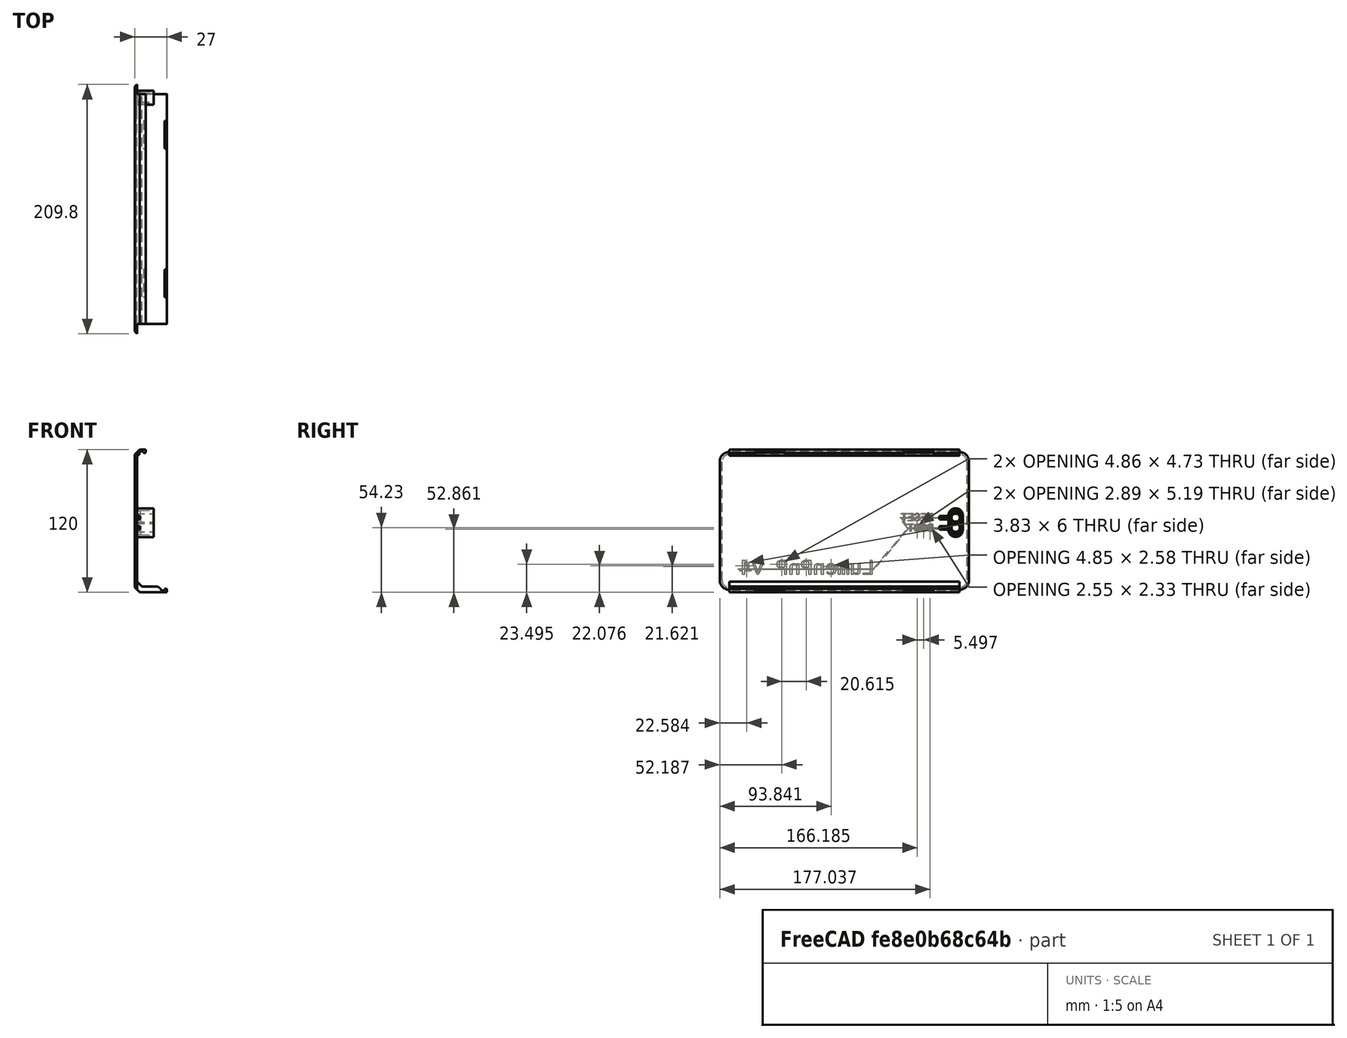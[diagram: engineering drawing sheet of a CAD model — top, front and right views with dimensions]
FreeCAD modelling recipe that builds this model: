
FCSTD DOCUMENT  (FreeCAD 0.20R29603 (Git))
Label: control-box-lid
License: Other
objects: Sketcher::SketchObject×17, PartDesign::Pocket×15, PartDesign::Pad×6, PartDesign::Plane×5, PartDesign::Fillet×5, Part::Part2DObjectPython×3, PartDesign::Mirrored×3, PartDesign::Chamfer×2, PartDesign::SubShapeBinder×2, PartDesign::Body×2, PartDesign::SubtractivePipe×1, Part::Compound×1
note: 91 computed .brp shape members not serialized (recipe doc carries the construction recipe); baked Part::Feature solids carry a one-line shape summary decoded from their .brp

FEATURE [PartDesign::Plane] DatumPlane003  label="Button Strike Plane"
  AttachmentOffset = pos=(0,0,-11.141) rot=(0,0,1;0rad)
  Length = 273.968
  MapMode = 5
  Placement = pos=(0,11.141,2.5e-15) rot=(1,0,0;1.5708rad)
  ResizeMode = 0
  Support = -> [XZ_Plane001]
  Width = 182.068
FEATURE [PartDesign::Plane] DatumPlane004  label="Print Plane"
  AttachmentOffset = pos=(0,0,27) rot=(-0.707107,0,-0.707107;0rad)
  Length = 273.968
  MapMode = 5
  Placement = pos=(0,27,6e-15) rot=(0,0.707107,0.707107;3.14159rad)
  ResizeMode = 0
  Support = -> [XZ_Plane001]
  Width = 182.068
FEATURE [PartDesign::Plane] DatumPlane005
  Length = 69.3666
  MapMode = 5
  Placement = pos=(0,0,0) rot=(0.57735,0.57735,0.57735;2.0944rad)
  ResizeMode = 0
  Support = -> [YZ_Plane001]
  Width = 162.367
FEATURE [Part::Part2DObjectPython] ShapeString  label="LumenPnP Text"  # Draft 2D object (typed FeaturePython)
  AttachmentOffset = pos=(-132,15,0) rot=(0,0,1;0rad)
  FontFile = <userpath>/Github/lumenpnp/lib/fonts/RobotoMono-VariableFont_weight.ttf
  MakeFace = true
  MapMode = 2
  Placement = pos=(132,27,15) rot=(0,0.707107,0.707107;3.14159rad)
  Size = 15
  String = LumenPnP v4
  Support = -> [DatumPlane004]
  Tracking = 0
FEATURE [Part::Part2DObjectPython] ShapeString002  # Draft 2D object (typed FeaturePython)
  AttachmentOffset = pos=(-182,51,0) rot=(0,0,1;0rad)
  FontFile = <userpath>/Github/lumenpnp/lib/fonts/RobotoMono-VariableFont_weight.ttf
  MakeFace = true
  MapMode = 2
  Placement = pos=(182,27,51) rot=(0,0.707107,0.707107;3.14159rad)
  Size = 8
  String = BOOT
  Support = -> [DatumPlane004]
  Tracking = 0
FEATURE [Part::Part2DObjectPython] ShapeString003  # Draft 2D object (typed FeaturePython)
  AttachmentOffset = pos=(-182,60,0) rot=(0,0,1;0rad)
  FontFile = <userpath>/Github/lumenpnp/lib/fonts/RobotoMono-VariableFont_weight.ttf
  MakeFace = true
  MapMode = 2
  Placement = pos=(182,27,60) rot=(0,0.707107,0.707107;3.14159rad)
  Size = 8
  String = RESET
  Support = -> [DatumPlane004]
  Tracking = 0
FEATURE [Sketcher::SketchObject] Sketch
  FullyConstrained = true
  MapMode = 5
  Placement = pos=(0,0,0) rot=(1,0,0;1.5708rad)
  Support = -> [XZ_Plane001]
  sketch-geometry (4):
    g0: LineSegment StartX=0 StartY=0 StartZ=0 EndX=214 EndY=0 EndZ=0
    g1: LineSegment StartX=214 StartY=0 StartZ=0 EndX=214 EndY=120 EndZ=0
    g2: LineSegment StartX=214 StartY=120 StartZ=0 EndX=0 EndY=120 EndZ=0
    g3: LineSegment StartX=0 StartY=120 StartZ=0 EndX=0 EndY=0 EndZ=0
  constraints (11):
    c: Coincident(g0,g1)
    c: Coincident(g1,g2)
    c: Coincident(g2,g3)
    c: Coincident(g3,g0)
    c: Horizontal(g0)
    c: Horizontal(g2)
    c: Vertical(g1)
    c: Vertical(g3)
    c: Coincident(g0,g-1)
    c: DistanceX(g0,g0) = 214
    c: DistanceY(g3,g3) = 120
FEATURE [PartDesign::Pad] Pad  label="Bulk Profile"
  Direction = (0,-1,-2e-16)
  Length = 27
  Length2 = 10
  Placement = pos=(0,0,0) rot=(1,0,0;1.5708rad)
  Profile = -> Sketch
  ReferenceAxis = -> Sketch [N_Axis]
  Reversed = true
  Type = 0
FEATURE [PartDesign::Fillet] Fillet  label="Round Bulk Profile Edges"
  Base = -> Pad [Edge8,Edge5,Edge2,Edge1]
  BaseFeature = -> Pad
  Placement = pos=(0,0,0) rot=(1,0,0;1.5708rad)
  Radius = 10
  SupportTransform = false
  UseAllEdges = false
FEATURE [Sketcher::SketchObject] Sketch001
  ExternalGeometry = -> [Sketch]
  FullyConstrained = true
  MapMode = 5
  Placement = pos=(0,0,0) rot=(1,0,0;1.5708rad)
  Support = -> [XZ_Plane001]
  sketch-geometry (12):
    g0: LineSegment StartX=-50 StartY=109.1 StartZ=0 EndX=250 EndY=109.1 EndZ=0
    g1: LineSegment StartX=250 StartY=109.1 StartZ=0 EndX=250 EndY=10.9 EndZ=0
    g2: LineSegment StartX=250 StartY=10.9 StartZ=0 EndX=-50 EndY=10.9 EndZ=0
    g3: LineSegment StartX=-50 StartY=10.9 StartZ=0 EndX=-50 EndY=109.1 EndZ=0
    g4: ArcOfCircle CenterX=-50 CenterY=109.1 CenterZ=0 NormalX=0 NormalY=0 NormalZ=1 AngleXU=0 Radius=6 StartAngle=1.5708 EndAngle=3.14159
    g5: ArcOfCircle CenterX=250 CenterY=109.1 CenterZ=0 NormalX=0 NormalY=0 NormalZ=1 AngleXU=0 Radius=6 StartAngle=0 EndAngle=1.5708
    g6: ArcOfCircle CenterX=250 CenterY=10.9 CenterZ=0 NormalX=0 NormalY=0 NormalZ=1 AngleXU=0 Radius=6 StartAngle=4.71239 EndAngle=6.28319
    g7: ArcOfCircle CenterX=-50 CenterY=10.9 CenterZ=0 NormalX=0 NormalY=0 NormalZ=1 AngleXU=0 Radius=6 StartAngle=3.14159 EndAngle=4.71239
    g8: LineSegment StartX=-56 StartY=109.1 StartZ=0 EndX=-56 EndY=10.9 EndZ=0
    g9: LineSegment StartX=-50 StartY=4.9 StartZ=0 EndX=250 EndY=4.9 EndZ=0
    g10: LineSegment StartX=256 StartY=10.9 StartZ=0 EndX=256 EndY=109.1 EndZ=0
    g11: LineSegment StartX=250 StartY=115.1 StartZ=0 EndX=-50 EndY=115.1 EndZ=0
  constraints (32):
    c: Coincident(g0,g1)
    c: Coincident(g1,g2)
    c: Coincident(g2,g3)
    c: Coincident(g3,g0)
    c: Horizontal(g0)
    c: Horizontal(g2)
    c: Vertical(g1)
    c: Vertical(g3)
    c: Coincident(g4,g0)
    c: Coincident(g5,g0)
    c: Coincident(g6,g1)
    c: Coincident(g7,g2)
    c: Vertical(g8)
    c: Horizontal(g9)
    c: Vertical(g10)
    c: Tangent(g11,g4) = -1.5708
    c: Tangent(g8,g4) = -1.5708
    c: Tangent(g8,g7) = -1.5708
    c: Tangent(g9,g7) = -1.5708
    c: Tangent(g9,g6) = -1.5708
    c: Tangent(g10,g6) = -1.5708
    c: Tangent(g10,g5) = -1.5708
    c: Tangent(g11,g5) = -1.5708
    c: DistanceX(g2,g2) = 300
    c: DistanceX(g-1,g7) = -50
    c: DistanceY(g-1,g7) = 10.9
    c: DistanceY(g3,g3) = 98.2
    c: Diameter(g4) = 12
    c: DistanceX(g5,g-3) = -42
    c: DistanceX(g-1,g6) = 250
    c: DistanceY(g4,g4) = 6
    c: DistanceY(g7,g7) = 6
FEATURE [PartDesign::Pocket] Pocket  label="Hollow Out Bulk Body"
  BaseFeature = -> Fillet
  Direction = (0,1,2e-16)
  Length = 25
  Length2 = 5
  Placement = pos=(0,0,0) rot=(1,0,0;1.5708rad)
  Profile = -> Sketch001
  ReferenceAxis = -> Sketch001 [N_Axis]
  Type = 0
FEATURE [PartDesign::Chamfer] Chamfer  label="Internal Chamfer"
  Angle = 45
  Base = -> Pocket [Edge21,Edge27]
  BaseFeature = -> Pocket
  ChamferType = 0
  FlipDirection = false
  Placement = pos=(0,0,0) rot=(1,0,0;1.5708rad)
  Size = 4
  Size2 = 1
  SupportTransform = false
  UseAllEdges = false
FEATURE [Sketcher::SketchObject] Sketch011  label="LumenPnP Icon"
  AttachmentOffset = pos=(136,87,-26) rot=(0,0,1;0rad)
  FullyConstrained = true
  MapMode = 5
  Placement = pos=(136,26,87) rot=(1,0,0;1.5708rad)
  Support = -> [XZ_Plane001]
  sketch-geometry (26):
    g0: LineSegment StartX=-123.5 StartY=-76 StartZ=0 EndX=-109.5 EndY=-76 EndZ=0
    g1: LineSegment StartX=-109.5 StartY=-76 StartZ=0 EndX=-109.5 EndY=-60 EndZ=0
    g2: LineSegment StartX=-109.5 StartY=-60 StartZ=0 EndX=14 EndY=-60 EndZ=0
    g3: LineSegment StartX=14 StartY=-60 StartZ=0 EndX=14 EndY=-76 EndZ=0
    g4: LineSegment StartX=14 StartY=-76 StartZ=0 EndX=28 EndY=-76 EndZ=0
    g5: LineSegment StartX=28 StartY=-76 StartZ=0 EndX=28 EndY=-42 EndZ=0
    g6: LineSegment StartX=28 StartY=-42 StartZ=0 EndX=-2.5 EndY=-11.5 EndZ=0
    g7: LineSegment StartX=-2.5 StartY=-11.5 StartZ=0 EndX=-29.75 EndY=-11.5 EndZ=0
    g8: LineSegment StartX=-29.75 StartY=-11.5 StartZ=0 EndX=-29.75 EndY=-1.5 EndZ=0
    g9: LineSegment StartX=-29.75 StartY=-1.5 StartZ=0 EndX=-47.75 EndY=16.5 EndZ=0
    g10: LineSegment StartX=-47.75 StartY=16.5 StartZ=0 EndX=-95 EndY=16.5 EndZ=0
    g11: LineSegment StartX=-123.5 StartY=-76 StartZ=0 EndX=-123.5 EndY=-12 EndZ=0
    g12: LineSegment StartX=-115.5 StartY=-34 StartZ=0 EndX=-115.5 EndY=-12 EndZ=0
    g13: LineSegment StartX=-115.5 StartY=-34 StartZ=0 EndX=-93 EndY=-11.5 EndZ=0
    g14: LineSegment StartX=-93 StartY=-11.5 StartZ=0 EndX=-65.75 EndY=-11.5 EndZ=0
    g15: LineSegment StartX=-65.75 StartY=-11.5 StartZ=0 EndX=-65.75 EndY=-1.5 EndZ=0
    g16: LineSegment StartX=-65.75 StartY=-1.5 StartZ=0 EndX=-55.75 EndY=8.5 EndZ=0
    g17: LineSegment StartX=-55.75 StartY=8.5 StartZ=0 EndX=-95 EndY=8.5 EndZ=0
    g18: ArcOfCircle CenterX=-95 CenterY=-12 CenterZ=0 NormalX=0 NormalY=0 NormalZ=1 AngleXU=0 Radius=20.5 StartAngle=1.5708 EndAngle=3.14159
    g19: ArcOfCircle CenterX=-95 CenterY=-12 CenterZ=0 NormalX=0 NormalY=0 NormalZ=1 AngleXU=0 Radius=28.5 StartAngle=1.5708 EndAngle=3.14159
    g20: Ellipse CenterX=-47.75 CenterY=-38 CenterZ=0 NormalX=0 NormalY=0 NormalZ=1 MajorRadius=19 MinorRadius=8 AngleXU=0
    g21: LineSegment StartX=-28.75 StartY=-38 StartZ=0 EndX=-66.75 EndY=-38 EndZ=0
    g22: LineSegment StartX=-47.75 StartY=-30 StartZ=0 EndX=-47.75 EndY=-46 EndZ=0
    g23: GeomPoint X=-30.5163 Y=-38 Z=0
    g24: GeomPoint X=-64.9837 Y=-38 Z=0
    g25: LineSegment StartX=-47.75 StartY=-60 StartZ=0 EndX=-47.75 EndY=16.5 EndZ=0
  constraints (69):
    c: Horizontal(g0)
    c: Coincident(g0,g1)
    c: Vertical(g1)
    c: Coincident(g1,g2)
    c: Horizontal(g2)
    c: Coincident(g2,g3)
    c: Vertical(g3)
    c: Coincident(g3,g4)
    c: Horizontal(g4)
    c: Coincident(g4,g5)
    c: Vertical(g5)
    c: Coincident(g5,g6)
    c: Coincident(g6,g7)
    c: Horizontal(g7)
    c: Coincident(g7,g8)
    c: Vertical(g8)
    c: Coincident(g8,g9)
    c: Coincident(g9,g10)
    c: Horizontal(g10)
    c: Coincident(g0,g11)
    c: Vertical(g11)
    c: Vertical(g12)
    c: Coincident(g12,g13)
    c: Coincident(g13,g14)
    c: Horizontal(g14)
    c: Coincident(g14,g15)
    c: Vertical(g15)
    c: Coincident(g15,g16)
    c: Coincident(g16,g17)
    c: Horizontal(g17)
    c: Coincident(g18,g17)
    c: Coincident(g18,g12)
    c: Coincident(g19,g10)
    c: Coincident(g19,g11)
    c: InternalAlignment(g21-g24 -> g20) x4
    c: DistanceY(g22,g22) = 16
    c: DistanceX(g21,g21) = 38
    c: Horizontal(g21)
    c: Tangent(g19,g10)
    c: Tangent(g18,g17)
    c: Tangent(g18,g12)
    c: Tangent(g19,g11)
    c: Angle(g9,g8) = 2.35619
    c: Angle(g15,g16) = 2.35619
    c: DistanceX(g0,g0) = 14
    c: DistanceX(g4,g4) = 14
    c: DistanceX(g2,g2) = 123.5
    c: DistanceY(g1,g1) = 16
    c: DistanceY(g3,g3) = 16
    c: DistanceY(g5,g5) = 34
    c: Angle(g6,g5) = 2.35619
    c: DistanceX(g0,g-1) = 123.5
    c: DistanceY(g0,g-1) = 76
    c: Angle(g13,g14) = 2.35619
    c: Coincident(g25,g9)
    c: Vertical(g25)
    c: Symmetric(g1,g2,g25)
    c: PointOnObject(g20,g25)
    c: Distance(g7,g25) = 18
    c: Distance(g14,g25) = 18
    c: PointOnObject(g7,g14)
    c: DistanceY(g0,g13) = 64.5
    c: DistanceX(g0,g12) = 8
    c: DistanceY(g25,g25) = 76.5
    c: Equal(g8,g15)
    c: Coincident(g18,g19)
    c: Diameter(g19) = 57
    c: Equal(g7,g14)
    c: DistanceY(g25,g20) = 22
FEATURE [Sketcher::SketchObject] Sketch013
  FullyConstrained = false
  MapMode = 5
  Placement = pos=(0,11.141,2.5e-15) rot=(0,0.707107,0.707107;3.14159rad)
  Support = -> [DatumPlane003]
  sketch-geometry (2):
    g0: Circle CenterX=-200.672 CenterY=54.1904 CenterZ=0 NormalX=0 NormalY=0 NormalZ=1 AngleXU=0 Radius=3.5
    g1: Circle CenterX=-200.672 CenterY=62.6904 CenterZ=0 NormalX=0 NormalY=0 NormalZ=1 AngleXU=0 Radius=3.5
  constraints (4):
    c: Diameter(g0) = 7
    c: Vertical(g1,g0)
    c: Equal(g0,g1)
    c: DistanceY(g0,g1) = 8.5
FEATURE [PartDesign::Pad] Pad003  label="Button Forming"
  BaseFeature = -> Chamfer
  Direction = (0,1,2e-16)
  Length = 10
  Length2 = 10
  Placement = pos=(0,0,0) rot=(1,0,0;1.5708rad)
  Profile = -> Sketch013
  ReferenceAxis = -> Sketch013 [N_Axis]
  Type = 2
FEATURE [Sketcher::SketchObject] Sketch014
  ExternalGeometry = -> [Pad003]
  FullyConstrained = true
  MapMode = 5
  Placement = pos=(0,11.141,2.5e-15) rot=(1,0,0;1.5708rad)
  Support = -> [DatumPlane003]
  sketch-geometry (20):
    g0: ArcOfCircle CenterX=200.672 CenterY=62.6904 CenterZ=0 NormalX=0 NormalY=0 NormalZ=1 AngleXU=0 Radius=4 StartAngle=3.52599 EndAngle=9.04038
    g1: ArcOfCircle CenterX=200.672 CenterY=62.6904 CenterZ=0 NormalX=0 NormalY=0 NormalZ=1 AngleXU=0 Radius=3.5 StartAngle=3.43134 EndAngle=9.13503
    g2: ArcOfCircle CenterX=200.672 CenterY=54.1904 CenterZ=0 NormalX=0 NormalY=0 NormalZ=1 AngleXU=0 Radius=3.5 StartAngle=3.43134 EndAngle=9.13503
    g3: ArcOfCircle CenterX=200.672 CenterY=54.1904 CenterZ=0 NormalX=0 NormalY=0 NormalZ=1 AngleXU=0 Radius=4 StartAngle=3.52599 EndAngle=9.04038
    g4: ArcOfCircle CenterX=186.964 CenterY=62.6904 CenterZ=0 NormalX=0 NormalY=0 NormalZ=1 AngleXU=0 Radius=1.5 StartAngle=1.5708 EndAngle=4.71239
    g5: LineSegment StartX=186.964 StartY=61.1904 StartZ=0 EndX=196.964 EndY=61.1904 EndZ=0
    g6: ArcOfCircle CenterX=186.964 CenterY=54.1904 CenterZ=0 NormalX=0 NormalY=0 NormalZ=1 AngleXU=0 Radius=1.5 StartAngle=1.5708 EndAngle=4.71239
    g7: LineSegment StartX=196.964 StartY=55.6904 StartZ=0 EndX=186.964 EndY=55.6904 EndZ=0
    g8: LineSegment StartX=186.964 StartY=52.6904 StartZ=0 EndX=196.964 EndY=52.6904 EndZ=0
    g9: LineSegment StartX=196.964 StartY=64.1904 StartZ=0 EndX=186.964 EndY=64.1904 EndZ=0
    g10: ArcOfCircle CenterX=186.964 CenterY=62.6904 CenterZ=0 NormalX=0 NormalY=0 NormalZ=1 AngleXU=0 Radius=1 StartAngle=1.5708 EndAngle=4.71239
    g11: LineSegment StartX=186.964 StartY=61.6904 StartZ=0 EndX=197.318 EndY=61.6904 EndZ=0
    g12: LineSegment StartX=197.318 StartY=63.6904 StartZ=0 EndX=186.964 EndY=63.6904 EndZ=0
    g13: LineSegment StartX=186.964 StartY=63.6904 StartZ=0 EndX=186.964 EndY=64.1904 EndZ=0
    g14: LineSegment StartX=186.964 StartY=61.6904 StartZ=0 EndX=186.964 EndY=61.1904 EndZ=0
    g15: LineSegment StartX=186.964 StartY=62.6904 StartZ=0 EndX=200.672 EndY=62.6904 EndZ=0
    g16: LineSegment StartX=186.964 StartY=53.1904 StartZ=0 EndX=197.318 EndY=53.1904 EndZ=0
    g17: LineSegment StartX=197.318 StartY=55.1904 StartZ=0 EndX=186.964 EndY=55.1904 EndZ=0
    g18: LineSegment StartX=186.964 StartY=55.1904 StartZ=0 EndX=186.964 EndY=55.6904 EndZ=0
    g19: LineSegment StartX=186.964 StartY=53.1904 StartZ=0 EndX=186.964 EndY=52.6904 EndZ=0
  constraints (54):
    c: Coincident(g1,g0)
    c: Coincident(g3,g2)
    c: Equal(g1,g2)
    c: Diameter(g1) = 7
    c: Diameter(g3) = 8
    c: Diameter(g0) = 8
    c: Coincident(g9,g4) = -1.5708
    c: Tangent(g4,g5) = -1.5708
    c: Tangent(g7,g6) = -1.5708
    c: Tangent(g6,g8) = -1.5708
    c: Horizontal(g7)
    c: Equal(g6,g4)
    c: Coincident(g5,g0)
    c: Coincident(g9,g0)
    c: Tangent(g10,g11) = -1.5708
    c: Tangent(g12,g10) = -1.5708
    c: Coincident(g10,g4)
    c: Horizontal(g11)
    c: Coincident(g13,g12)
    c: Coincident(g13,g9)
    c: Vertical(g13)
    c: Coincident(g14,g11)
    c: Coincident(g14,g5)
    c: Vertical(g14)
    c: Coincident(g11,g1)
    c: Horizontal(g9)
    c: DistanceY(g13,g13) = 0.5
    c: Coincident(g15,g4)
    c: Coincident(g15,g0)
    c: Horizontal(g15)
    c: DistanceX(g9,g9) = 10
    c: Diameter(g10) = 2
    c: Vertical(g6,g4)
    c: Coincident(g3,g7)
    c: Coincident(g8,g3)
    c: Equal(g9,g7)
    c: Horizontal(g16)
    c: Horizontal(g17)
    c: Symmetric(g17,g16,g6)
    c: Coincident(g18,g17)
    c: Coincident(g18,g7)
    c: Coincident(g19,g16)
    c: Coincident(g19,g8)
    c: Tangent(g18,g19)
    c: Coincident(g2,g17)
    c: Coincident(g2,g16)
    c: DistanceY(g18,g18) = 0.5
    c: Coincident(g1,g12)
    c: Horizontal(g12)
    c: DistanceY(g2,g0) = 8.5
    c: Vertical(g15,g2)
    c: DistanceX(g-1,g2) = 200.672
    c: DistanceY(g-1,g2) = 54.1904
    c: Coincident(g2,g-3)
FEATURE [PartDesign::Pocket] Pocket016  label="Button Clearance"
  BaseFeature = -> Pad003
  Direction = (0,1,2e-16)
  Length = 40
  Length2 = 5
  Midplane = true
  Placement = pos=(0,0,0) rot=(1,0,0;1.5708rad)
  Profile = -> Sketch014
  ReferenceAxis = -> Sketch014 [N_Axis]
  Type = 0
FEATURE [PartDesign::Pocket] Pocket020  label="Boot"
  BaseFeature = -> Pocket016
  Direction = (0,-1,-2e-16)
  Length = 0.8
  Length2 = 5
  Placement = pos=(0,0,0) rot=(1,0,0;1.5708rad)
  Profile = -> ShapeString002
  ReferenceAxis = -> ShapeString002 [N_Axis]
  Type = 0
FEATURE [PartDesign::Pocket] Pocket021  label="Reset"
  BaseFeature = -> Pocket020
  Direction = (0,-1,-2e-16)
  Length = 0.8
  Length2 = 5
  Placement = pos=(0,0,0) rot=(1,0,0;1.5708rad)
  Profile = -> ShapeString003
  ReferenceAxis = -> ShapeString003 [N_Axis]
  Type = 0
FEATURE [Sketcher::SketchObject] Sketch023
  AttachmentOffset = pos=(0,0,-10.859) rot=(0,0,1;0rad)
  FullyConstrained = true
  MapMode = 5
  Placement = pos=(0,22,4.9e-15) rot=(1,0,0;1.5708rad)
  Support = -> [DatumPlane003]
  sketch-geometry (10):
    g0: LineSegment StartX=186.964 StartY=61.45 StartZ=0 EndX=197.414 EndY=61.45 EndZ=0
    g1: LineSegment StartX=197.414 StartY=61.45 StartZ=0 EndX=197.414 EndY=63.95 EndZ=0
    g2: LineSegment StartX=197.414 StartY=63.95 StartZ=0 EndX=186.964 EndY=63.95 EndZ=0
    g3: LineSegment StartX=186.964 StartY=63.95 StartZ=0 EndX=186.964 EndY=61.45 EndZ=0
    g4: LineSegment StartX=186.964 StartY=52.95 StartZ=0 EndX=197.414 EndY=52.95 EndZ=0
    g5: LineSegment StartX=197.414 StartY=52.95 StartZ=0 EndX=197.414 EndY=55.45 EndZ=0
    g6: LineSegment StartX=197.414 StartY=55.45 StartZ=0 EndX=186.964 EndY=55.45 EndZ=0
    g7: LineSegment StartX=186.964 StartY=55.45 StartZ=0 EndX=186.964 EndY=52.95 EndZ=0
    g8: ArcOfCircle CenterX=200.683 CenterY=54.2 CenterZ=0 NormalX=0 NormalY=0 NormalZ=1 AngleXU=0 Radius=3.5 StartAngle=2.77639 EndAngle=3.5068
    g9: ArcOfCircle CenterX=200.683 CenterY=62.7 CenterZ=0 NormalX=0 NormalY=0 NormalZ=1 AngleXU=0 Radius=3.5 StartAngle=2.77639 EndAngle=3.5068
  constraints (29):
    c: Coincident(g0,g1)
    c: Coincident(g1,g2)
    c: Coincident(g2,g3)
    c: Coincident(g3,g0)
    c: Horizontal(g0)
    c: Horizontal(g2)
    c: Vertical(g1)
    c: Vertical(g3)
    c: Coincident(g4,g5)
    c: Coincident(g5,g6)
    c: Coincident(g6,g7)
    c: Coincident(g7,g4)
    c: Horizontal(g4)
    c: Horizontal(g6)
    c: Vertical(g5)
    c: Coincident(g8,g5)
    c: Coincident(g8,g4)
    c: Coincident(g9,g1)
    c: Coincident(g9,g0)
    c: Equal(g9,g8)
    c: Distance(g7) = 2.5
    c: Equal(g7,g3)
    c: Tangent(g7,g3)
    c: Distance(g4,g0) = 8.5
    c: Vertical(g8,g9)
    c: DistanceX(g2,g2) = 10.45
    c: Diameter(g9) = 7
    c: DistanceX(g-1,g4) = 186.964
    c: DistanceY(g-1,g4) = 52.95
FEATURE [PartDesign::Pocket] Pocket024  label="Make button more bendable"
  BaseFeature = -> Pocket021
  Direction = (0,1,2e-16)
  Length = 3.25
  Length2 = 5
  Placement = pos=(0,0,0) rot=(1,0,0;1.5708rad)
  Profile = -> Sketch023
  ReferenceAxis = -> Sketch023 [N_Axis]
  Type = 0
FEATURE [Sketcher::SketchObject] Sketch024
  ExternalGeometry = -> [Pocket024]
  FullyConstrained = true
  MapMode = 5
  Placement = pos=(0,11.141,2.5e-15) rot=(1,0,0;1.5708rad)
  Support = -> [DatumPlane003]
  sketch-geometry (20):
    g0: ArcOfCircle CenterX=200.672 CenterY=64.5 CenterZ=0 NormalX=0 NormalY=0 NormalZ=1 AngleXU=0 Radius=6 StartAngle=0 EndAngle=3.14159
    g1: ArcOfCircle CenterX=200.672 CenterY=52.5 CenterZ=0 NormalX=0 NormalY=0 NormalZ=1 AngleXU=0 Radius=6 StartAngle=3.14159 EndAngle=6.28319
    g2: LineSegment StartX=194.672 StartY=64.5 StartZ=0 EndX=194.672 EndY=52.5 EndZ=0
    g3: LineSegment StartX=206.672 StartY=52.5 StartZ=0 EndX=206.672 EndY=64.5 EndZ=0
    g4: ArcOfCircle CenterX=200.672 CenterY=64.5 CenterZ=0 NormalX=0 NormalY=0 NormalZ=1 AngleXU=0 Radius=4 StartAngle=9e-16 EndAngle=3.14159
    g5: ArcOfCircle CenterX=200.672 CenterY=52.5 CenterZ=0 NormalX=0 NormalY=0 NormalZ=1 AngleXU=0 Radius=4 StartAngle=3.14159 EndAngle=6.28319
    g6: LineSegment StartX=196.672 StartY=64.5 StartZ=0 EndX=196.672 EndY=52.5 EndZ=0
    g7: LineSegment StartX=204.672 StartY=52.5 StartZ=0 EndX=204.672 EndY=64.5 EndZ=0
    g8: LineSegment StartX=194.672 StartY=64.5 StartZ=0 EndX=206.672 EndY=64.5 EndZ=0
    g9: LineSegment StartX=206.672 StartY=64.5 StartZ=0 EndX=206.672 EndY=66.8 EndZ=0
    g10: LineSegment StartX=202.672 StartY=70.8 StartZ=0 EndX=198.672 EndY=70.8 EndZ=0
    g11: LineSegment StartX=194.672 StartY=66.8 StartZ=0 EndX=194.672 EndY=64.5 EndZ=0
    g12: LineSegment StartX=194.672 StartY=52.5 StartZ=0 EndX=206.672 EndY=52.5 EndZ=0
    g13: LineSegment StartX=206.672 StartY=52.5 StartZ=0 EndX=206.672 EndY=50.2 EndZ=0
    g14: LineSegment StartX=202.672 StartY=46.2 StartZ=0 EndX=198.672 EndY=46.2 EndZ=0
    g15: LineSegment StartX=194.672 StartY=50.2 StartZ=0 EndX=194.672 EndY=52.5 EndZ=0
    g16: ArcOfCircle CenterX=198.672 CenterY=66.8 CenterZ=0 NormalX=0 NormalY=0 NormalZ=1 AngleXU=0 Radius=4 StartAngle=1.5708 EndAngle=3.14159
    g17: ArcOfCircle CenterX=202.672 CenterY=66.8 CenterZ=0 NormalX=0 NormalY=0 NormalZ=1 AngleXU=0 Radius=4 StartAngle=8e-16 EndAngle=1.5708
    g18: ArcOfCircle CenterX=202.672 CenterY=50.2 CenterZ=0 NormalX=0 NormalY=0 NormalZ=1 AngleXU=0 Radius=4 StartAngle=4.71239 EndAngle=6.28319
    g19: ArcOfCircle CenterX=198.672 CenterY=50.2 CenterZ=0 NormalX=0 NormalY=0 NormalZ=1 AngleXU=0 Radius=4 StartAngle=3.14159 EndAngle=4.71239
  constraints (46):
    c: Tangent(g0,g2) = -1.5708
    c: Tangent(g2,g1) = -1.5708
    c: Tangent(g1,g3) = -1.5708
    c: Tangent(g3,g0) = -1.5708
    c: Equal(g0,g1)
    c: Vertical(g2)
    c: Tangent(g4,g6) = -1.5708
    c: Tangent(g6,g5) = -1.5708
    c: Tangent(g5,g7) = -1.5708
    c: Tangent(g7,g4) = -1.5708
    c: Equal(g4,g5)
    c: Coincident(g4,g0)
    c: Coincident(g5,g1)
    c: DistanceX(g0,g4) = 2
    c: Diameter(g4) = 8
    c: DistanceY(g1,g0) = 12
    c: DistanceX(g-1,g1) = 200.672
    c: DistanceY(g-1,g1) = 52.5
    c: Coincident(g8,g9)
    c: Coincident(g11,g8)
    c: Horizontal(g10)
    c: Vertical(g9)
    c: Vertical(g11)
    c: Coincident(g8,g2)
    c: Coincident(g8,g3)
    c: Coincident(g12,g13)
    c: Coincident(g15,g12)
    c: Horizontal(g14)
    c: Vertical(g13)
    c: Vertical(g15)
    c: Coincident(g12,g2)
    c: Coincident(g13,g3)
    c: Tangent(g11,g16) = -1.5708
    c: Tangent(g10,g16) = -1.5708
    c: Tangent(g9,g17) = -1.5708
    c: Tangent(g10,g17) = -1.5708
    c: Tangent(g14,g18) = 1.5708
    c: Tangent(g13,g18) = 1.5708
    c: Tangent(g15,g19) = 1.5708
    c: Tangent(g14,g19) = 1.5708
    c: Equal(g16,g17)
    c: Equal(g17,g18)
    c: Equal(g18,g19)
    c: Diameter(g19) = 8
    c: Equal(g15,g11)
    c: DistanceY(g2,g10) = 6.3
FEATURE [PartDesign::Pad] Pad004  label="Button Shield"
  BaseFeature = -> Pocket024
  Direction = (0,-1,-2e-16)
  Length = 14
  Length2 = 10
  Placement = pos=(0,0,0) rot=(1,0,0;1.5708rad)
  Profile = -> Sketch024
  ReferenceAxis = -> Sketch024 [N_Axis]
  Reversed = true
  Type = 3
  UpToFace = -> Pocket024 [Face2]
FEATURE [Sketcher::SketchObject] Sketch025
  AttachmentOffset = pos=(0,0,-5) rot=(0,0,1;0rad)
  FullyConstrained = true
  MapMode = 5
  Placement = pos=(0,22,4.9e-15) rot=(0,0.707107,0.707107;3.14159rad)
  Support = -> [DatumPlane004]
  sketch-geometry (8):
    g0: LineSegment StartX=-196.964 StartY=64.5 StartZ=0 EndX=-185.964 EndY=64.5 EndZ=0
    g1: LineSegment StartX=-185.964 StartY=64.5 StartZ=0 EndX=-185.964 EndY=60.5 EndZ=0
    g2: LineSegment StartX=-185.964 StartY=60.5 StartZ=0 EndX=-196.964 EndY=60.5 EndZ=0
    g3: LineSegment StartX=-196.964 StartY=60.5 StartZ=0 EndX=-196.964 EndY=64.5 EndZ=0
    g4: LineSegment StartX=-196.964 StartY=56 StartZ=0 EndX=-185.964 EndY=56 EndZ=0
    g5: LineSegment StartX=-185.964 StartY=56 StartZ=0 EndX=-185.964 EndY=52 EndZ=0
    g6: LineSegment StartX=-185.964 StartY=52 StartZ=0 EndX=-196.964 EndY=52 EndZ=0
    g7: LineSegment StartX=-196.964 StartY=52 StartZ=0 EndX=-196.964 EndY=56 EndZ=0
  constraints (23):
    c: Coincident(g0,g1)
    c: Coincident(g1,g2)
    c: Coincident(g2,g3)
    c: Coincident(g3,g0)
    c: Horizontal(g0)
    c: Horizontal(g2)
    c: Vertical(g1)
    c: Vertical(g3)
    c: Coincident(g4,g5)
    c: Coincident(g5,g6)
    c: Coincident(g6,g7)
    c: Coincident(g7,g4)
    c: Horizontal(g4)
    c: Horizontal(g6)
    c: Vertical(g7)
    c: DistanceX(g2,g2) = 11
    c: DistanceY(g1,g1) = 4
    c: Equal(g4,g0)
    c: Equal(g3,g7)
    c: DistanceY(g4,g2) = 4.5
    c: Tangent(g5,g1)
    c: DistanceX(g5,g-1) = 185.964
    c: DistanceY(g-1,g5) = 52
FEATURE [Sketcher::SketchObject] Sketch026
  FullyConstrained = true
  MapMode = 5
  Placement = pos=(0,0,0) rot=(-0.57735,0.57735,0.57735;4.18879rad)
  Support = -> [DatumPlane005]
  sketch-geometry (17):
    g0: LineSegment StartX=0 StartY=3 StartZ=0 EndX=-5 EndY=3 EndZ=0
    g1: LineSegment StartX=-5 StartY=3 StartZ=0 EndX=-5 EndY=5 EndZ=0
    g2: LineSegment StartX=-5 StartY=5 StartZ=0 EndX=0 EndY=5 EndZ=0
    g3: LineSegment StartX=0 StartY=5 StartZ=0 EndX=0 EndY=3 EndZ=0
    g4: ArcOfCircle CenterX=-3.5 CenterY=3 CenterZ=0 NormalX=0 NormalY=0 NormalZ=1 AngleXU=0 Radius=1.5 StartAngle=3.14159 EndAngle=5.79323
    g5: ArcOfCircle CenterX=-1 CenterY=1.66667 CenterZ=0 NormalX=0 NormalY=0 NormalZ=1 AngleXU=0 Radius=1.33333 StartAngle=1.5708 EndAngle=2.65164
    g6: LineSegment StartX=-1 StartY=3 StartZ=0 EndX=0 EndY=3 EndZ=0
    g7: ArcOfCircle CenterX=-3.5 CenterY=3 CenterZ=0 NormalX=0 NormalY=0 NormalZ=1 AngleXU=0 Radius=1.7 StartAngle=3.14159 EndAngle=5.79323
    g8: LineSegment StartX=-2 StartY=2.2 StartZ=0 EndX=-2.17647 EndY=2.29412 EndZ=0
    g9: ArcOfCircle CenterX=-1 CenterY=1.66667 CenterZ=0 NormalX=0 NormalY=0 NormalZ=1 AngleXU=0 Radius=1.13333 StartAngle=1.5708 EndAngle=2.65164
    g10: LineSegment StartX=-1 StartY=2.8 StartZ=0 EndX=0 EndY=2.8 EndZ=0
    g11: LineSegment StartX=0 StartY=2.8 StartZ=0 EndX=0 EndY=5 EndZ=0
    g12: LineSegment StartX=-5.2 StartY=3 StartZ=0 EndX=-5.2 EndY=5 EndZ=0
    g13: LineSegment StartX=-5 StartY=5 StartZ=0 EndX=-5.2 EndY=5 EndZ=0
    g14: LineSegment StartX=-4.70208 StartY=1.79792 StartZ=0 EndX=-7.90416 EndY=5 EndZ=0
    g15: LineSegment StartX=-5.2 StartY=5 StartZ=0 EndX=-7.90416 EndY=5 EndZ=0
    g16: ArcOfCircle CenterX=-3.5 CenterY=3 CenterZ=0 NormalX=0 NormalY=0 NormalZ=1 AngleXU=0 Radius=1.7 StartAngle=3.92699 EndAngle=5.79323
  constraints (47):
    c: Coincident(g0,g1)
    c: Coincident(g1,g2)
    c: Coincident(g2,g3)
    c: Coincident(g3,g0)
    c: Horizontal(g0)
    c: Horizontal(g2)
    c: Vertical(g1)
    c: Vertical(g3)
    c: PointOnObject(g0,g-2)
    c: Coincident(g4,g0)
    c: PointOnObject(g5,g0)
    c: Tangent(g4,g5) = 1.5708
    c: DistanceX(g5,g0) = 1
    c: DistanceX(g2,g2) = 5
    c: DistanceY(g-1,g2) = 5
    c: Vertical(g5,g5)
    c: Perpendicular(g4,g0)
    c: Diameter(g4) = 3
    c: Coincident(g6,g5)
    c: Coincident(g6,g3)
    c: DistanceY(g3,g3) = 2
    c: Coincident(g7,g4)
    c: Coincident(g8,g7)
    c: Coincident(g8,g5)
    c: Perpendicular(g7,g8)
    c: Coincident(g9,g7)
    c: Coincident(g5,g9)
    c: Vertical(g9,g5)
    c: Coincident(g10,g9)
    c: PointOnObject(g10,g-2)
    c: Horizontal(g10)
    c: Coincident(g11,g10)
    c: Coincident(g11,g2)
    c: Vertical(g12)
    c: Coincident(g13,g2)
    c: Coincident(g13,g12)
    c: Horizontal(g13)
    c: Distance(g8) = 0.2
    c: Tangent(g14,g7) = 1.5708
    c: Tangent(g12,g7) = 1.5708
    c: Angle(g14,g0) = 0.785398
    c: Coincident(g15,g12)
    c: Coincident(g15,g14)
    c: Horizontal(g15)
    c: Coincident(g16,g14)
    c: Coincident(g16,g9)
    c: Equal(g16,g7)
FEATURE [Sketcher::SketchObject] Sketch071
  AttachmentOffset = pos=(10,105,0) rot=(0,0,1;0rad)
  FullyConstrained = true
  MapMode = 5
  Placement = pos=(10,-2.33e-14,105) rot=(1,0,0;1.5708rad)
  Support = -> [XZ_Plane001]
  sketch-geometry (40):
    g0: ArcOfCircle CenterX=1.2e-15 CenterY=5 CenterZ=0 NormalX=0 NormalY=0 NormalZ=1 AngleXU=0 Radius=10 StartAngle=1.5708 EndAngle=3.14159
    g1: LineSegment StartX=-4e-16 StartY=15 StartZ=0 EndX=194 EndY=15 EndZ=0
    g2: ArcOfCircle CenterX=194 CenterY=5 CenterZ=0 NormalX=0 NormalY=0 NormalZ=1 AngleXU=0 Radius=10 StartAngle=1e-16 EndAngle=1.5708
    g3: LineSegment StartX=204 StartY=5 StartZ=0 EndX=204 EndY=-95 EndZ=0
    g4: ArcOfCircle CenterX=194 CenterY=-95 CenterZ=0 NormalX=0 NormalY=0 NormalZ=1 AngleXU=0 Radius=10 StartAngle=4.71239 EndAngle=6.28319
    g5: LineSegment StartX=194 StartY=-105 StartZ=0 EndX=0 EndY=-105 EndZ=0
    g6: ArcOfCircle CenterX=1.4e-15 CenterY=-95 CenterZ=0 NormalX=0 NormalY=0 NormalZ=1 AngleXU=0 Radius=10 StartAngle=3.14159 EndAngle=4.71239
    g7: LineSegment StartX=-10 StartY=-95 StartZ=0 EndX=-10 EndY=5 EndZ=0
    g8: GeomPoint X=-10 Y=15 Z=0
    g9: GeomPoint X=204 Y=-105 Z=0
    g10: ArcOfCircle CenterX=1.2e-15 CenterY=5 CenterZ=0 NormalX=0 NormalY=0 NormalZ=1 AngleXU=0 Radius=4.8 StartAngle=1.5708 EndAngle=3.14159
    g11: LineSegment StartX=-10 StartY=5 StartZ=0 EndX=-4.8 EndY=5 EndZ=0
    g12: LineSegment StartX=4e-16 StartY=9.8 StartZ=0 EndX=-4e-16 EndY=15 EndZ=0
    g13: ArcOfCircle CenterX=1.4e-15 CenterY=-95 CenterZ=0 NormalX=0 NormalY=0 NormalZ=1 AngleXU=0 Radius=4.8 StartAngle=3.14159 EndAngle=4.71239
    g14: ArcOfCircle CenterX=194 CenterY=5 CenterZ=0 NormalX=0 NormalY=0 NormalZ=1 AngleXU=0 Radius=4.8 StartAngle=3e-16 EndAngle=1.5708
    g15: ArcOfCircle CenterX=194 CenterY=-95 CenterZ=0 NormalX=0 NormalY=0 NormalZ=1 AngleXU=0 Radius=4.8 StartAngle=4.71239 EndAngle=6.28319
    g16: LineSegment StartX=198.8 StartY=5 StartZ=0 EndX=204 EndY=5 EndZ=0
    g17: LineSegment StartX=198.8 StartY=-95 StartZ=0 EndX=204 EndY=-95 EndZ=0
    g18: LineSegment StartX=-10 StartY=-95 StartZ=0 EndX=-4.8 EndY=-95 EndZ=0
    g19: LineSegment StartX=198.8 StartY=5 StartZ=0 EndX=198.8 EndY=-95 EndZ=0
    g20: LineSegment StartX=5e-16 StartY=-99.8 StartZ=0 EndX=-4e-16 EndY=-105 EndZ=0
    g21: LineSegment StartX=-4.8 StartY=-95 StartZ=0 EndX=-4.8 EndY=5 EndZ=0
    g22: LineSegment StartX=194 StartY=9.8 StartZ=0 EndX=194 EndY=15 EndZ=0
    g23: LineSegment StartX=194 StartY=-99.8 StartZ=0 EndX=194 EndY=-105 EndZ=0
    g24: LineSegment StartX=-4e-16 StartY=15 StartZ=0 EndX=0.2 EndY=15 EndZ=0
    g25: LineSegment StartX=0.2 StartY=15 StartZ=0 EndX=0.2 EndY=9.8 EndZ=0
    g26: LineSegment StartX=0.2 StartY=9.8 StartZ=0 EndX=4e-16 EndY=9.8 EndZ=0
    g27: LineSegment StartX=4e-16 StartY=9.8 StartZ=0 EndX=-4e-16 EndY=15 EndZ=0
    g28: LineSegment StartX=-4e-16 StartY=-105 StartZ=0 EndX=0.2 EndY=-105 EndZ=0
    g29: LineSegment StartX=0.2 StartY=-105 StartZ=0 EndX=0.2 EndY=-99.8 EndZ=0
    g30: LineSegment StartX=0.2 StartY=-99.8 StartZ=0 EndX=5e-16 EndY=-99.8 EndZ=0
    g31: LineSegment StartX=5e-16 StartY=-99.8 StartZ=0 EndX=-4e-16 EndY=-105 EndZ=0
    g32: LineSegment StartX=194 StartY=-99.8 StartZ=0 EndX=193.8 EndY=-99.8 EndZ=0
    g33: LineSegment StartX=193.8 StartY=-99.8 StartZ=0 EndX=193.8 EndY=-105 EndZ=0
    g34: LineSegment StartX=193.8 StartY=-105 StartZ=0 EndX=194 EndY=-105 EndZ=0
    g35: LineSegment StartX=194 StartY=-105 StartZ=0 EndX=194 EndY=-99.8 EndZ=0
    g36: LineSegment StartX=194 StartY=15 StartZ=0 EndX=193.8 EndY=15 EndZ=0
    g37: LineSegment StartX=193.8 StartY=15 StartZ=0 EndX=193.8 EndY=9.8 EndZ=0
    g38: LineSegment StartX=193.8 StartY=9.8 StartZ=0 EndX=194 EndY=9.8 EndZ=0
    g39: LineSegment StartX=194 StartY=9.8 StartZ=0 EndX=194 EndY=15 EndZ=0
  constraints (100):
    c: Tangent(g0,g1) = 1.5708
    c: Tangent(g1,g2) = 1.5708
    c: Tangent(g2,g3) = 1.5708
    c: Tangent(g3,g4) = 1.5708
    c: Tangent(g4,g5) = 1.5708
    c: Tangent(g5,g6) = 1.5708
    c: Tangent(g6,g7) = 1.5708
    c: Tangent(g7,g0) = 1.5708
    c: Horizontal(g1)
    c: Horizontal(g5)
    c: Vertical(g3)
    c: Vertical(g7)
    c: Equal(g0,g2)
    c: Equal(g2,g4)
    c: Equal(g4,g6)
    c: PointOnObject(g8,g1)
    c: PointOnObject(g8,g7)
    c: PointOnObject(g9,g3)
    c: PointOnObject(g9,g5)
    c: Diameter(g0) = 20
    c: PointOnObject(g0,g-2)
    c: DistanceY(g5,g0) = 120
    c: DistanceX(g0,g2) = 214
    c: DistanceY(g-1,g0) = 15
    c: Coincident(g10,g0)
    c: PointOnObject(g10,g-2)
    c: Horizontal(g10,g0)
    c: Coincident(g11,g0)
    c: Coincident(g11,g10)
    c: Coincident(g12,g10)
    c: Coincident(g12,g0)
    c: Diameter(g10) = 9.6
    c: Coincident(g13,g6)
    c: PointOnObject(g13,g-2)
    c: Coincident(g14,g2)
    c: Coincident(g15,g4)
    c: Coincident(g16,g14)
    c: Coincident(g16,g2)
    c: Horizontal(g16)
    c: Coincident(g17,g15)
    c: Coincident(g17,g4)
    c: Horizontal(g17)
    c: Coincident(g18,g6)
    c: Coincident(g18,g13)
    c: Horizontal(g18)
    c: Equal(g10,g14)
    c: Equal(g14,g15)
    c: Equal(g15,g13)
    c: Coincident(g19,g14)
    c: PointOnObject(g19,g15)
    c: Vertical(g19)
    c: Coincident(g20,g13)
    c: Coincident(g20,g6)
    c: Vertical(g20)
    c: Coincident(g21,g13)
    c: Coincident(g21,g10)
    c: Coincident(g22,g14)
    c: Coincident(g22,g2)
    c: Vertical(g22)
    c: Coincident(g23,g15)
    c: Coincident(g23,g4)
    c: Vertical(g23)
    c: Coincident(g24,g25)
    c: Coincident(g25,g26)
    c: Coincident(g26,g27)
    c: Coincident(g27,g24)
    c: Horizontal(g24)
    c: Horizontal(g26)
    c: Vertical(g25)
    c: Coincident(g24,g0)
    c: Coincident(g26,g10)
    c: Coincident(g28,g29)
    c: Coincident(g29,g30)
    c: Coincident(g30,g31)
    c: Coincident(g31,g28)
    c: Horizontal(g28)
    c: Horizontal(g30)
    c: Coincident(g28,g6)
    c: Coincident(g13,g30)
    c: Coincident(g32,g33)
    c: Coincident(g33,g34)
    c: Coincident(g34,g35)
    c: Coincident(g35,g32)
    c: Horizontal(g32)
    c: Horizontal(g34)
    c: Vertical(g33)
    c: Coincident(g32,g15)
    c: Coincident(g34,g4)
    c: Coincident(g36,g37)
    c: Coincident(g37,g38)
    c: Coincident(g38,g39)
    c: Coincident(g39,g36)
    c: Horizontal(g36)
    c: Horizontal(g38)
    c: Coincident(g36,g2)
    c: Coincident(g14,g38)
    c: Tangent(g37,g33)
    c: Tangent(g29,g25)
    c: Equal(g24,g36)
    c: DistanceX(g34,g34) = 0.2
FEATURE [PartDesign::Plane] DatumPlane
  AttachmentOffset = pos=(0,0,107) rot=(0,0,1;0rad)
  Length = 69.3666
  MapMode = 5
  Placement = pos=(107,-2.38e-14,2.38e-14) rot=(0.57735,0.57735,0.57735;2.0944rad)
  ResizeMode = 0
  Support = -> [YZ_Plane001]
  Width = 162.367
FEATURE [PartDesign::Plane] DatumPlane007
  AttachmentOffset = pos=(0,0,60) rot=(0,0,1;0rad)
  Length = 259.098
  MapMode = 5
  Placement = pos=(0,0,60) rot=(0,0,1;0rad)
  ResizeMode = 0
  Support = -> [XY_Plane001]
  Width = 74.198
FEATURE [Sketcher::SketchObject] Sketch068
  AttachmentOffset = pos=(204,-8.2,2.878) rot=(1,0,0;0.593412rad)
  FullyConstrained = false
  MapMode = 5
  Placement = pos=(204,-8.2,2.878) rot=(1,0,0;0.593412rad)
  Support = -> [XY_Plane001]
  sketch-geometry (26):
    g0: LineSegment StartX=-22 StartY=0 StartZ=0 EndX=-47 EndY=0 EndZ=0
    g1: LineSegment StartX=-47 StartY=0 StartZ=0 EndX=-47 EndY=4.5 EndZ=0
    g2: LineSegment StartX=-39.5 StartY=12 StartZ=0 EndX=-29.5 EndY=12 EndZ=0
    g3: LineSegment StartX=-22 StartY=4.5 StartZ=0 EndX=-22 EndY=0 EndZ=0
    g4: LineSegment StartX=-147 StartY=0 StartZ=0 EndX=-172 EndY=0 EndZ=0
    g5: LineSegment StartX=-172 StartY=0 StartZ=0 EndX=-172 EndY=4.5 EndZ=0
    g6: LineSegment StartX=-164.5 StartY=12 StartZ=0 EndX=-154.5 EndY=12 EndZ=0
    g7: LineSegment StartX=-147 StartY=4.5 StartZ=0 EndX=-147 EndY=0 EndZ=0
    g8: ArcOfCircle CenterX=-29.5 CenterY=4.5 CenterZ=0 NormalX=0 NormalY=0 NormalZ=1 AngleXU=0 Radius=7.5 StartAngle=0 EndAngle=1.5708
    g9: GeomPoint X=-22 Y=12 Z=0
    g10: ArcOfCircle CenterX=-39.5 CenterY=4.5 CenterZ=0 NormalX=0 NormalY=0 NormalZ=1 AngleXU=0 Radius=7.5 StartAngle=1.5708 EndAngle=3.14159
    g11: GeomPoint X=-47 Y=12 Z=0
    g12: ArcOfCircle CenterX=-154.5 CenterY=4.5 CenterZ=0 NormalX=0 NormalY=0 NormalZ=1 AngleXU=0 Radius=7.5 StartAngle=0 EndAngle=1.5708
    g13: GeomPoint X=-147 Y=12 Z=0
    g14: ArcOfCircle CenterX=-164.5 CenterY=4.5 CenterZ=0 NormalX=0 NormalY=0 NormalZ=1 AngleXU=0 Radius=7.5 StartAngle=1.5708 EndAngle=3.14159
    g15: GeomPoint X=-172 Y=12 Z=0
    g16: LineSegment StartX=-22 StartY=0 StartZ=0 EndX=-47 EndY=0 EndZ=0
    g17: LineSegment StartX=-47 StartY=0 StartZ=0 EndX=-47 EndY=-3 EndZ=0
    g18: LineSegment StartX=-47 StartY=-3 StartZ=0 EndX=-22 EndY=-3 EndZ=0
    g19: LineSegment StartX=-22 StartY=-3 StartZ=0 EndX=-22 EndY=0 EndZ=0
    g20: LineSegment StartX=-147 StartY=0 StartZ=0 EndX=-172 EndY=0 EndZ=0
    g21: LineSegment StartX=-172 StartY=0 StartZ=0 EndX=-172 EndY=-3 EndZ=0
    g22: LineSegment StartX=-172 StartY=-3 StartZ=0 EndX=-147 EndY=-3 EndZ=0
    g23: LineSegment StartX=-147 StartY=-3 StartZ=0 EndX=-147 EndY=0 EndZ=0
    g24: LineSegment StartX=10 StartY=38 StartZ=0 EndX=-204 EndY=38 EndZ=0
    g25: LineSegment StartX=-97 StartY=38 StartZ=0 EndX=-97 EndY=-62.3515 EndZ=0
  constraints (63):
    c: Coincident(g0,g1)
    c: Coincident(g3,g0)
    c: Horizontal(g0)
    c: Horizontal(g2)
    c: Vertical(g1)
    c: Vertical(g3)
    c: PointOnObject(g0,g-1)
    c: Coincident(g4,g5)
    c: Coincident(g7,g4)
    c: Horizontal(g4)
    c: Horizontal(g6)
    c: Vertical(g5)
    c: Vertical(g7)
    c: PointOnObject(g4,g-1)
    c: PointOnObject(g9,g3)
    c: PointOnObject(g9,g2)
    c: Tangent(g3,g8) = 1.5708
    c: Tangent(g2,g8) = 1.5708
    c: PointOnObject(g11,g2)
    c: PointOnObject(g11,g1)
    c: Tangent(g2,g10) = 1.5708
    c: Tangent(g1,g10) = 1.5708
    c: PointOnObject(g13,g7)
    c: PointOnObject(g13,g6)
    c: Tangent(g7,g12) = 1.5708
    c: Tangent(g6,g12) = 1.5708
    c: PointOnObject(g15,g6)
    c: PointOnObject(g15,g5)
    c: Tangent(g6,g14) = 1.5708
    c: Tangent(g5,g14) = 1.5708
    c: Equal(g14,g12)
    c: Equal(g12,g10)
    c: Equal(g10,g8)
    c: Equal(g3,g2)
    c: Equal(g2,g6)
    c: Equal(g1,g7)
    c: Diameter(g8) = 15
    c: DistanceX(g0,g0) = 25
    c: DistanceY(g0,g2) = 12
    c: Coincident(g16,g17)
    c: Coincident(g17,g18)
    c: Coincident(g18,g19)
    c: Coincident(g19,g16)
    c: Horizontal(g18)
    c: Vertical(g17)
    c: Vertical(g19)
    c: Coincident(g16,g3)
    c: Coincident(g20,g21)
    c: Coincident(g21,g22)
    c: Coincident(g22,g23)
    c: Coincident(g23,g20)
    c: Vertical(g21)
    c: Vertical(g23)
    c: Coincident(g20,g7)
    c: Coincident(g5,g21)
    c: Coincident(g1,g17)
    c: Tangent(g22,g18)
    c: DistanceY(g-1,g17) = -3
    c: DistanceX(g22,g17) = 100
    c: DistanceX(g-1,g24) = 10
    c: DistanceX(g24,g24) = 214
    c: Symmetric(g24,g24,g25)
    c: Symmetric(g1,g7,g25)
FEATURE [PartDesign::Pocket] Pocket029
  BaseFeature = -> Pad004
  Direction = (0,-1,6e-16)
  Length = 2
  Length2 = 5
  Placement = pos=(0,0,0) rot=(1,0,0;1.5708rad)
  Profile = -> Pad004 [Face221,Face218]
  Type = 0
FEATURE [PartDesign::Chamfer] Chamfer001
  Angle = 3
  Base = -> Pocket029 [Edge684]
  BaseFeature = -> Pocket029
  ChamferType = 2
  FlipDirection = true
  Placement = pos=(0,0,0) rot=(1,0,0;1.5708rad)
  Size = 11
  Size2 = 1
  SupportTransform = false
  UseAllEdges = false
FEATURE [PartDesign::Pocket] Pocket025  label="Locking Lip"
  BaseFeature = -> Chamfer001
  Direction = (1,-1e-16,1e-16)
  Length = 5
  Length2 = 5
  Placement = pos=(0,0,0) rot=(1,0,0;1.5708rad)
  Profile = -> Sketch026
  ReferenceAxis = -> Sketch026 [N_Axis]
  Type = 1
FEATURE [PartDesign::Pocket] Pocket026  label="Removing Side"
  BaseFeature = -> Pocket025
  Direction = (0,1,2e-16)
  Length = 25
  Length2 = 5
  Placement = pos=(0,0,0) rot=(1,0,0;1.5708rad)
  Profile = -> Sketch071
  ReferenceAxis = -> Sketch071 [N_Axis]
  Type = 0
FEATURE [PartDesign::Mirrored] Mirrored001  label="Mirrors Removing Side"
  BaseFeature = -> Pocket026
  MirrorPlane = -> DatumPlane
  Originals = -> [Pocket026]
  Placement = pos=(0,0,0) rot=(1,0,0;1.5708rad)
FEATURE [PartDesign::Mirrored] Mirrored002  label="Mirrors Locking Lip"
  BaseFeature = -> Mirrored001
  MirrorPlane = -> DatumPlane007
  Originals = -> [Pocket025]
  Placement = pos=(0,0,0) rot=(1,0,0;1.5708rad)
  Refine = true
FEATURE [PartDesign::Pocket] Pocket027
  BaseFeature = -> Mirrored002
  Direction = (0,-1,-2e-16)
  Length = 0.8
  Length2 = 5
  Placement = pos=(0,0,0) rot=(1,0,0;1.5708rad)
  Profile = -> ShapeString
  ReferenceAxis = -> ShapeString [N_Axis]
  Type = 0
FEATURE [PartDesign::Pocket] Pocket028
  BaseFeature = -> Pocket027
  Direction = (0,0.559193,-0.829038)
  Length = 6
  Length2 = 5
  Placement = pos=(0,0,0) rot=(1,0,0;1.5708rad)
  Profile = -> Sketch068
  ReferenceAxis = -> Sketch068 [N_Axis]
  Type = 0
FEATURE [PartDesign::Mirrored] Mirrored
  BaseFeature = -> Pocket028
  MirrorPlane = -> DatumPlane007
  Originals = -> [Pocket028]
  Placement = pos=(0,0,0) rot=(1,0,0;1.5708rad)
FEATURE [PartDesign::Pocket] Pocket030
  BaseFeature = -> Mirrored
  Direction = (0,1.1e-15,1)
  Length = 5
  Length2 = 5
  Placement = pos=(0,0,0) rot=(1,0,0;1.5708rad)
  Profile = -> Mirrored [Face3,Face2,Face8,Edge28,Face7]
  ReferenceAxis = -> Mirrored [Edge48]
  Reversed = true
  Type = 0
FEATURE [PartDesign::Pocket] Pocket031
  BaseFeature = -> Pocket030
  Direction = (0,1.2e-15,1)
  Length = 5
  Length2 = 5
  Placement = pos=(0,0,0) rot=(1,0,0;1.5708rad)
  Profile = -> Mirrored [Face29,Face30,Face18,Face19]
  ReferenceAxis = -> Pocket030 [Edge11]
  Type = 0
FEATURE [PartDesign::Fillet] Fillet001
  Base = -> Pocket031 [Edge230,Edge625]
  BaseFeature = -> Pocket031
  Placement = pos=(0,0,0) rot=(1,0,0;1.5708rad)
  Radius = 5
  SupportTransform = false
  UseAllEdges = false
FEATURE [PartDesign::Fillet] Fillet002
  Base = -> Fillet001 [Edge36,Edge40,Edge28,Edge1383,Edge1379,Edge1375]
  BaseFeature = -> Fillet001
  Placement = pos=(0,0,0) rot=(1,0,0;1.5708rad)
  Radius = 0.6
  Refine = true
  SupportTransform = false
  UseAllEdges = false
FEATURE [Sketcher::SketchObject] Sketch069
  AttachmentOffset = pos=(-204,105,-10) rot=(0,0,1;0rad)
  FullyConstrained = true
  MapMode = 5
  Placement = pos=(10,204,105) rot=(-0.57735,0.57735,0.57735;4.18879rad)
  Support = -> [YZ_Plane001]
  sketch-geometry (6):
    g0: LineSegment StartX=177 StartY=15 StartZ=0 EndX=177 EndY=10.9 EndZ=0
    g1: LineSegment StartX=177 StartY=10.9 StartZ=0 EndX=181.1 EndY=15 EndZ=0
    g2: LineSegment StartX=177 StartY=15 StartZ=0 EndX=181.1 EndY=15 EndZ=0
    g3: LineSegment StartX=177 StartY=-100.9 StartZ=0 EndX=177 EndY=-105 EndZ=0
    g4: LineSegment StartX=177 StartY=-105 StartZ=0 EndX=181.1 EndY=-105 EndZ=0
    g5: LineSegment StartX=177 StartY=-100.9 StartZ=0 EndX=181.1 EndY=-105 EndZ=0
  constraints (18):
    c: Vertical(g0)
    c: Coincident(g1,g0)
    c: Coincident(g2,g0)
    c: Coincident(g2,g1)
    c: Coincident(g4,g3)
    c: Horizontal(g4)
    c: Coincident(g5,g3)
    c: Coincident(g5,g4)
    c: Equal(g5,g1)
    c: Horizontal(g2)
    c: Equal(g0,g2)
    c: Equal(g2,g3)
    c: DistanceX(g3,g4) = 4.1
    c: DistanceX(g3,g-1) = -177
    c: Tangent(g0,g3)
    c: DistanceY(g3,g0) = 120
    c: DistanceX(g-2,g3) = 177
    c: DistanceY(g3,g-1) = 105
FEATURE [Sketcher::SketchObject] Sketch072
  AttachmentOffset = pos=(-204,105,27) rot=(0,0,1;0rad)
  FullyConstrained = true
  MapMode = 5
  Placement = pos=(204,27,105) rot=(0,0.707107,0.707107;3.14159rad)
  Support = -> [XZ_Plane001]
  sketch-geometry (10):
    g0: ArcOfCircle CenterX=1.2e-15 CenterY=5 CenterZ=0 NormalX=0 NormalY=0 NormalZ=1 AngleXU=0 Radius=10 StartAngle=1.5708 EndAngle=3.14159
    g1: LineSegment StartX=-4e-16 StartY=15 StartZ=0 EndX=194 EndY=15 EndZ=0
    g2: ArcOfCircle CenterX=194 CenterY=5 CenterZ=0 NormalX=0 NormalY=0 NormalZ=1 AngleXU=0 Radius=10 StartAngle=1e-16 EndAngle=1.5708
    g3: LineSegment StartX=204 StartY=5 StartZ=0 EndX=204 EndY=-95 EndZ=0
    g4: ArcOfCircle CenterX=194 CenterY=-95 CenterZ=0 NormalX=0 NormalY=0 NormalZ=1 AngleXU=0 Radius=10 StartAngle=4.71239 EndAngle=6.28319
    g5: LineSegment StartX=194 StartY=-105 StartZ=0 EndX=0 EndY=-105 EndZ=0
    g6: ArcOfCircle CenterX=1.7e-15 CenterY=-95 CenterZ=0 NormalX=0 NormalY=0 NormalZ=1 AngleXU=0 Radius=10 StartAngle=3.14159 EndAngle=4.71239
    g7: LineSegment StartX=-10 StartY=-95 StartZ=0 EndX=-10 EndY=5 EndZ=0
    g8: GeomPoint X=-10 Y=15 Z=0
    g9: GeomPoint X=204 Y=-105 Z=0
  constraints (24):
    c: Tangent(g0,g1) = 1.5708
    c: Tangent(g1,g2) = 1.5708
    c: Tangent(g2,g3) = 1.5708
    c: Tangent(g3,g4) = 1.5708
    c: Tangent(g4,g5) = 1.5708
    c: Tangent(g5,g6) = 1.5708
    c: Tangent(g6,g7) = 1.5708
    c: Tangent(g7,g0) = 1.5708
    c: Horizontal(g1)
    c: Horizontal(g5)
    c: Vertical(g3)
    c: Vertical(g7)
    c: Equal(g0,g2)
    c: Equal(g2,g4)
    c: Equal(g4,g6)
    c: PointOnObject(g8,g1)
    c: PointOnObject(g8,g7)
    c: PointOnObject(g9,g3)
    c: PointOnObject(g9,g5)
    c: Diameter(g0) = 20
    c: PointOnObject(g0,g-2)
    c: DistanceY(g5,g0) = 120
    c: DistanceX(g0,g2) = 214
    c: DistanceY(g-1,g0) = 15
FEATURE [PartDesign::SubtractivePipe] SubtractivePipe
  AuxilleryCurvelinear = true
  AuxillerySpineTangent = false
  BaseFeature = -> Fillet002
  Binormal = (0,0,0)
  Mode = 0
  Placement = pos=(0,0,0) rot=(1,0,0;1.5708rad)
  Profile = -> Sketch069
  Spine = -> Sketch072
  SpineTangent = false
  Transformation = 0
  Transition = 0
FEATURE [Sketcher::SketchObject] Sketch073
  AttachmentOffset = pos=(17.9,120,0) rot=(0,0,1;3.14159rad)
  FullyConstrained = false
  MapMode = 5
  Placement = pos=(-1.13e-14,17.9,120) rot=(0.57735,-0.57735,0.57735;4.18879rad)
  Support = -> [DatumPlane005]
  sketch-geometry (23):
    g0: LineSegment StartX=0 StartY=3 StartZ=0 EndX=-5 EndY=3 EndZ=0
    g1: LineSegment StartX=-5 StartY=3 StartZ=0 EndX=-5 EndY=5 EndZ=0
    g2: LineSegment StartX=-5 StartY=5 StartZ=0 EndX=0 EndY=5 EndZ=0
    g3: LineSegment StartX=0 StartY=5 StartZ=0 EndX=0 EndY=3 EndZ=0
    g4: ArcOfCircle CenterX=-3.5 CenterY=3 CenterZ=0 NormalX=0 NormalY=0 NormalZ=1 AngleXU=0 Radius=1.5 StartAngle=3.14159 EndAngle=5.79323
    g5: ArcOfCircle CenterX=-1 CenterY=1.66667 CenterZ=0 NormalX=0 NormalY=0 NormalZ=1 AngleXU=0 Radius=1.33333 StartAngle=1.5708 EndAngle=2.65164
    g6: LineSegment StartX=-1 StartY=3 StartZ=0 EndX=0 EndY=3 EndZ=0
    g7: ArcOfCircle CenterX=-3.5 CenterY=3 CenterZ=0 NormalX=0 NormalY=0 NormalZ=1 AngleXU=0 Radius=1.7 StartAngle=3.14159 EndAngle=5.79323
    g8: LineSegment StartX=-2 StartY=2.2 StartZ=0 EndX=-2.17647 EndY=2.29412 EndZ=0
    g9: ArcOfCircle CenterX=-1 CenterY=1.66667 CenterZ=0 NormalX=0 NormalY=0 NormalZ=1 AngleXU=0 Radius=1.13333 StartAngle=1.5708 EndAngle=2.65164
    g10: LineSegment StartX=-1 StartY=2.8 StartZ=0 EndX=0 EndY=2.8 EndZ=0
    g11: LineSegment StartX=0 StartY=2.8 StartZ=0 EndX=0 EndY=5 EndZ=0
    g12: LineSegment StartX=-5.2 StartY=3 StartZ=0 EndX=-5.2 EndY=5 EndZ=0
    g13: LineSegment StartX=-5 StartY=5 StartZ=0 EndX=-5.2 EndY=5 EndZ=0
    g14: LineSegment StartX=-4.70208 StartY=1.79792 StartZ=0 EndX=-7.90416 EndY=5 EndZ=0
    g15: LineSegment StartX=-5.2 StartY=5 StartZ=0 EndX=-7.90416 EndY=5 EndZ=0
    g16: ArcOfCircle CenterX=-3.5 CenterY=3 CenterZ=0 NormalX=0 NormalY=0 NormalZ=1 AngleXU=0 Radius=1.7 StartAngle=3.92699 EndAngle=5.79323
    g17: LineSegment StartX=-5.2 StartY=5 StartZ=0 EndX=-7.1 EndY=5 EndZ=0
    g18: LineSegment StartX=-7.1 StartY=5 StartZ=0 EndX=-7.1 EndY=9.41763 EndZ=0
    g19: LineSegment StartX=-7.1 StartY=9.41763 StartZ=0 EndX=19.0777 EndY=9.41763 EndZ=0
    g20: LineSegment StartX=19.0777 StartY=9.41763 StartZ=0 EndX=19.0777 EndY=-4.93334 EndZ=0
    g21: LineSegment StartX=0 StartY=2.8 StartZ=0 EndX=0 EndY=-4.93334 EndZ=0
    g22: LineSegment StartX=0 StartY=-4.93334 StartZ=0 EndX=19.0777 EndY=-4.93334 EndZ=0
  constraints (61):
    c: Coincident(g0,g1)
    c: Coincident(g1,g2)
    c: Coincident(g2,g3)
    c: Coincident(g3,g0)
    c: Horizontal(g0)
    c: Horizontal(g2)
    c: Vertical(g1)
    c: Vertical(g3)
    c: PointOnObject(g0,g-2)
    c: Coincident(g4,g0)
    c: PointOnObject(g5,g0)
    c: Tangent(g4,g5) = 1.5708
    c: DistanceX(g5,g0) = 1
    c: DistanceX(g2,g2) = 5
    c: DistanceY(g-1,g2) = 5
    c: Vertical(g5,g5)
    c: Perpendicular(g4,g0)
    c: Diameter(g4) = 3
    c: Coincident(g6,g5)
    c: Coincident(g6,g3)
    c: DistanceY(g3,g3) = 2
    c: Coincident(g7,g4)
    c: Coincident(g8,g7)
    c: Coincident(g8,g5)
    c: Perpendicular(g7,g8)
    c: Coincident(g9,g7)
    c: Coincident(g5,g9)
    c: Vertical(g9,g5)
    c: Coincident(g10,g9)
    c: PointOnObject(g10,g-2)
    c: Horizontal(g10)
    c: Coincident(g11,g10)
    c: Coincident(g11,g2)
    c: Vertical(g12)
    c: Coincident(g13,g2)
    c: Coincident(g13,g12)
    c: Horizontal(g13)
    c: Distance(g8) = 0.2
    c: Tangent(g14,g7) = 1.5708
    c: Tangent(g12,g7) = 1.5708
    c: Angle(g14,g0) = 0.785398
    c: Coincident(g15,g12)
    c: Coincident(g15,g14)
    c: Horizontal(g15)
    c: Coincident(g16,g14)
    c: Coincident(g16,g9)
    c: Equal(g16,g7)
    c: Coincident(g17,g12)
    c: Horizontal(g17)
    c: Coincident(g18,g17)
    c: Vertical(g18)
    c: Coincident(g19,g18)
    c: Horizontal(g19)
    c: Coincident(g20,g19)
    c: Vertical(g20)
    c: Coincident(g21,g10)
    c: PointOnObject(g21,g-2)
    c: Coincident(g22,g21)
    c: Coincident(g20,g22)
    c: DistanceX(g-2,g18) = -7.1
    c: Horizontal(g22)
FEATURE [PartDesign::Pocket] Pocket032
  BaseFeature = -> SubtractivePipe
  Direction = (-1,1e-16,-1e-16)
  Length = 5
  Length2 = 5
  Placement = pos=(0,0,0) rot=(1,0,0;1.5708rad)
  Profile = -> Sketch073
  ReferenceAxis = -> Sketch073 [N_Axis]
  Reversed = true
  Type = 1
FEATURE [PartDesign::Fillet] Fillet003
  Base = -> Pocket032 [Edge1503]
  BaseFeature = -> Pocket032
  Placement = pos=(0,0,0) rot=(1,0,0;1.5708rad)
  Radius = 0.6
  SupportTransform = false
  UseAllEdges = false
FEATURE [PartDesign::Fillet] Fillet004
  Base = -> Fillet003 [Edge25]
  BaseFeature = -> Fillet003
  Placement = pos=(0,0,0) rot=(1,0,0;1.5708rad)
  Radius = 1.89
  SupportTransform = false
  UseAllEdges = false
FEATURE [Sketcher::SketchObject] Sketch074
  AttachmentOffset = pos=(-10,9.7,-117.122) rot=(1,0,0;0.593412rad)
  FullyConstrained = false
  MapMode = 5
  Placement = pos=(10,9.7,117.122) rot=(0,0.956305,-0.292372;3.14159rad)
  Support = -> [XY_Plane001]
  expr: .AttachmentOffset.Base.y = -8.199999999999999 + 17.9
  expr: .AttachmentOffset.Base.z = 2.878 - 120
  sketch-geometry (26):
    g0: LineSegment StartX=-22 StartY=0 StartZ=0 EndX=-47 EndY=0 EndZ=0
    g1: LineSegment StartX=-47 StartY=0 StartZ=0 EndX=-47 EndY=4.5 EndZ=0
    g2: LineSegment StartX=-39.5 StartY=12 StartZ=0 EndX=-29.5 EndY=12 EndZ=0
    g3: LineSegment StartX=-22 StartY=4.5 StartZ=0 EndX=-22 EndY=0 EndZ=0
    g4: LineSegment StartX=-147 StartY=0 StartZ=0 EndX=-172 EndY=0 EndZ=0
    g5: LineSegment StartX=-172 StartY=0 StartZ=0 EndX=-172 EndY=4.5 EndZ=0
    g6: LineSegment StartX=-164.5 StartY=12 StartZ=0 EndX=-154.5 EndY=12 EndZ=0
    g7: LineSegment StartX=-147 StartY=4.5 StartZ=0 EndX=-147 EndY=0 EndZ=0
    g8: ArcOfCircle CenterX=-29.5 CenterY=4.5 CenterZ=0 NormalX=0 NormalY=0 NormalZ=1 AngleXU=0 Radius=7.5 StartAngle=0 EndAngle=1.5708
    g9: GeomPoint X=-22 Y=12 Z=0
    g10: ArcOfCircle CenterX=-39.5 CenterY=4.5 CenterZ=0 NormalX=0 NormalY=0 NormalZ=1 AngleXU=0 Radius=7.5 StartAngle=1.5708 EndAngle=3.14159
    g11: GeomPoint X=-47 Y=12 Z=0
    g12: ArcOfCircle CenterX=-154.5 CenterY=4.5 CenterZ=0 NormalX=0 NormalY=0 NormalZ=1 AngleXU=0 Radius=7.5 StartAngle=0 EndAngle=1.5708
    g13: GeomPoint X=-147 Y=12 Z=0
    g14: ArcOfCircle CenterX=-164.5 CenterY=4.5 CenterZ=0 NormalX=0 NormalY=0 NormalZ=1 AngleXU=0 Radius=7.5 StartAngle=1.5708 EndAngle=3.14159
    g15: GeomPoint X=-172 Y=12 Z=0
    g16: LineSegment StartX=-22 StartY=0 StartZ=0 EndX=-47 EndY=0 EndZ=0
    g17: LineSegment StartX=-47 StartY=0 StartZ=0 EndX=-47 EndY=-3 EndZ=0
    g18: LineSegment StartX=-47 StartY=-3 StartZ=0 EndX=-22 EndY=-3 EndZ=0
    g19: LineSegment StartX=-22 StartY=-3 StartZ=0 EndX=-22 EndY=0 EndZ=0
    g20: LineSegment StartX=-147 StartY=0 StartZ=0 EndX=-172 EndY=0 EndZ=0
    g21: LineSegment StartX=-172 StartY=0 StartZ=0 EndX=-172 EndY=-3 EndZ=0
    g22: LineSegment StartX=-172 StartY=-3 StartZ=0 EndX=-147 EndY=-3 EndZ=0
    g23: LineSegment StartX=-147 StartY=-3 StartZ=0 EndX=-147 EndY=0 EndZ=0
    g24: LineSegment StartX=10 StartY=38 StartZ=0 EndX=-204 EndY=38 EndZ=0
    g25: LineSegment StartX=-97 StartY=38 StartZ=0 EndX=-97 EndY=-62.3515 EndZ=0
  constraints (63):
    c: Coincident(g0,g1)
    c: Coincident(g3,g0)
    c: Horizontal(g0)
    c: Horizontal(g2)
    c: Vertical(g1)
    c: Vertical(g3)
    c: PointOnObject(g0,g-1)
    c: Coincident(g4,g5)
    c: Coincident(g7,g4)
    c: Horizontal(g4)
    c: Horizontal(g6)
    c: Vertical(g5)
    c: Vertical(g7)
    c: PointOnObject(g4,g-1)
    c: PointOnObject(g9,g3)
    c: PointOnObject(g9,g2)
    c: Tangent(g3,g8) = 1.5708
    c: Tangent(g2,g8) = 1.5708
    c: PointOnObject(g11,g2)
    c: PointOnObject(g11,g1)
    c: Tangent(g2,g10) = 1.5708
    c: Tangent(g1,g10) = 1.5708
    c: PointOnObject(g13,g7)
    c: PointOnObject(g13,g6)
    c: Tangent(g7,g12) = 1.5708
    c: Tangent(g6,g12) = 1.5708
    c: PointOnObject(g15,g6)
    c: PointOnObject(g15,g5)
    c: Tangent(g6,g14) = 1.5708
    c: Tangent(g5,g14) = 1.5708
    c: Equal(g14,g12)
    c: Equal(g12,g10)
    c: Equal(g10,g8)
    c: Equal(g3,g2)
    c: Equal(g2,g6)
    c: Equal(g1,g7)
    c: Diameter(g8) = 15
    c: DistanceX(g0,g0) = 25
    c: DistanceY(g0,g2) = 12
    c: Coincident(g16,g17)
    c: Coincident(g17,g18)
    c: Coincident(g18,g19)
    c: Coincident(g19,g16)
    c: Horizontal(g18)
    c: Vertical(g17)
    c: Vertical(g19)
    c: Coincident(g16,g3)
    c: Coincident(g20,g21)
    c: Coincident(g21,g22)
    c: Coincident(g22,g23)
    c: Coincident(g23,g20)
    c: Vertical(g21)
    c: Vertical(g23)
    c: Coincident(g20,g7)
    c: Coincident(g5,g21)
    c: Coincident(g1,g17)
    c: Tangent(g22,g18)
    c: DistanceY(g-1,g17) = -3
    c: DistanceX(g22,g17) = 100
    c: DistanceX(g-1,g24) = 10
    c: DistanceX(g24,g24) = 214
    c: Symmetric(g24,g24,g25)
    c: Symmetric(g1,g7,g25)
FEATURE [PartDesign::Pocket] Pocket033
  BaseFeature = -> Fillet004
  Direction = (0,0.559193,0.829038)
  Length = 6
  Length2 = 5
  Placement = pos=(0,0,0) rot=(1,0,0;1.5708rad)
  Profile = -> Sketch074
  ReferenceAxis = -> Sketch074 [N_Axis]
  Refine = true
  Type = 0
FEATURE [PartDesign::SubShapeBinder] Binder
  BindCopyOnChange = 0
  BindMode = 0
  ClaimChildren = false
  Context = -> Body [Binder.]
  Fuse = false
  MakeFace = true
  OffsetFill = false
  OffsetIntersection = false
  OffsetJoinType = 0
  OffsetOpenResult = false
  PartialLoad = false
  Relative = true
  Support = -> [Body001[Pocket033.Face435,Pocket033.Face434,Pocket033.Face433,Pocket033.Face432,Pocket033.Face431,Pocket033.Face430,Pocket033.Face429,Pocket033.Face428]]
  _Version = 2
FEATURE [Sketcher::SketchObject] Sketch075
  FullyConstrained = false
  MapMode = 5
  Placement = pos=(-64.284,1.43e-14,0) rot=(-0.57735,0.57735,0.57735;4.18879rad)
  Support = -> [Binder]
  sketch-geometry (13):
    g0: LineSegment StartX=-161.754 StartY=-60.8182 StartZ=0 EndX=-47.7382 EndY=-60.8182 EndZ=0
    g1: LineSegment StartX=-47.7382 StartY=-60.8182 StartZ=0 EndX=-47.7382 EndY=-60.3668 EndZ=0
    g2: LineSegment StartX=-47.7382 StartY=-60.3668 StartZ=0 EndX=-161.754 EndY=-60.3668 EndZ=0
    g3: LineSegment StartX=-218.054 StartY=-25.8537 StartZ=0 EndX=-190.957 EndY=-25.8537 EndZ=0
    g4: LineSegment StartX=-190.806 StartY=-26.4288 StartZ=0 EndX=-218.054 EndY=-26.4288 EndZ=0
    g5: LineSegment StartX=-218.054 StartY=-26.4288 StartZ=0 EndX=-218.054 EndY=-25.8537 EndZ=0
    g6: LineSegment StartX=-218.054 StartY=-17.6619 StartZ=0 EndX=-184.83 EndY=-17.6619 EndZ=0
    g7: LineSegment StartX=-183.556 StartY=-17.0868 StartZ=0 EndX=-218.054 EndY=-17.0868 EndZ=0
    g8: LineSegment StartX=-218.054 StartY=-17.0868 StartZ=0 EndX=-218.054 EndY=-17.6619 EndZ=0
    g9: LineSegment StartX=-190.806 StartY=-26.4288 StartZ=0 EndX=-161.754 EndY=-60.8182 EndZ=0
    g10: LineSegment StartX=-161.754 StartY=-60.3668 StartZ=0 EndX=-190.401 EndY=-26.2385 EndZ=0
    g11: LineSegment StartX=-184.83 StartY=-17.6619 StartZ=0 EndX=-190.957 EndY=-25.8537 EndZ=0
    g12: LineSegment StartX=-190.401 StartY=-26.2385 StartZ=0 EndX=-183.556 EndY=-17.0868 EndZ=0
  constraints (24):
    c: Coincident(g0,g1)
    c: Coincident(g1,g2)
    c: Horizontal(g0)
    c: Horizontal(g2)
    c: Vertical(g1)
    c: Coincident(g4,g5)
    c: Coincident(g5,g3)
    c: Horizontal(g3)
    c: Horizontal(g4)
    c: Vertical(g5)
    c: Coincident(g7,g8)
    c: Coincident(g8,g6)
    c: Horizontal(g6)
    c: Horizontal(g7)
    c: Equal(g5,g8)
    c: Tangent(g5,g8)
    c: Coincident(g9,g0)
    c: Coincident(g10,g2)
    c: Coincident(g11,g3)
    c: Coincident(g6,g11)
    c: Coincident(g4,g9)
    c: Coincident(g12,g10)
    c: Coincident(g7,g12)
    c: Parallel(g11,g12)
FEATURE [PartDesign::Pad] Pad005
  Direction = (-1,1e-16,1e-16)
  Length = 0.05
  Length2 = 10
  Profile = -> Sketch075
  ReferenceAxis = -> Sketch075 [N_Axis]
  Reversed = true
  Type = 0
FEATURE [PartDesign::Pad] Pad006
  BaseFeature = -> Pad005
  Direction = (-1,2e-16,0)
  Length = 0.8
  Length2 = 10
  Profile = -> Binder
  Type = 0
FEATURE [Sketcher::SketchObject] Sketch076
  ExternalGeometry = -> [Pocket033]
  FullyConstrained = false
  MapMode = 5
  Placement = pos=(0,27,5.9e-15) rot=(-1,0,0;1.5708rad)
  Support = -> [Pocket033]
  sketch-geometry (8):
    g0: LineSegment StartX=186.964 StartY=-53.0457 StartZ=0 EndX=197.188 EndY=-53.0457 EndZ=0
    g1: LineSegment StartX=197.188 StartY=-55.3572 StartZ=0 EndX=186.964 EndY=-55.3572 EndZ=0
    g2: LineSegment StartX=186.964 StartY=-55.3572 StartZ=0 EndX=186.964 EndY=-53.0457 EndZ=0
    g3: LineSegment StartX=186.964 StartY=-61.3918 StartZ=0 EndX=197.188 EndY=-61.3918 EndZ=0
    g4: LineSegment StartX=197.188 StartY=-64.0427 StartZ=0 EndX=186.964 EndY=-64.0427 EndZ=0
    g5: LineSegment StartX=186.964 StartY=-64.0427 StartZ=0 EndX=186.964 EndY=-61.3918 EndZ=0
    g6: ArcOfCircle CenterX=200.696 CenterY=-62.7173 CenterZ=0 NormalX=0 NormalY=0 NormalZ=1 AngleXU=0 Radius=3.75 StartAngle=3.50286 EndAngle=9.06351
    g7: ArcOfCircle CenterX=200.696 CenterY=-54.2014 CenterZ=0 NormalX=0 NormalY=0 NormalZ=1 AngleXU=0 Radius=3.69342 StartAngle=3.45985 EndAngle=9.10652
  constraints (21):
    c: Coincident(g1,g2)
    c: Coincident(g2,g0)
    c: Horizontal(g0)
    c: Horizontal(g1)
    c: Vertical(g2)
    c: PointOnObject(g0,g-4)
    c: Coincident(g4,g5)
    c: Coincident(g5,g3)
    c: Horizontal(g3)
    c: Horizontal(g4)
    c: Vertical(g5)
    c: PointOnObject(g3,g-3)
    c: Coincident(g7,g0)
    c: Coincident(g7,g1)
    c: Coincident(g6,g3)
    c: Coincident(g6,g4)
    c: Vertical(g7,g6)
    c: Vertical(g3,g1)
    c: Vertical(g0,g3)
    c: Diameter(g6) = 7.5
    c: Vertical(g4,g3)
FEATURE [PartDesign::Pocket] Pocket034
  BaseFeature = -> Pocket033
  Direction = (0,-1,-2e-16)
  Length = 0.8
  Length2 = 5
  Placement = pos=(0,0,0) rot=(1,0,0;1.5708rad)
  Profile = -> Sketch076
  ReferenceAxis = -> Sketch076 [N_Axis]
  Type = 0
FEATURE [PartDesign::Body] Body001  label="Base Lid"
  Group = -> [Sketch,Pad,Fillet,Sketch001,Pocket,Chamfer,ShapeString,Sketch011,DatumPlane003,Sketch013,Pad003,Sketch014,Pocket016,DatumPlane004,ShapeString002,ShapeString003,Pocket020,Pocket021,Sketch023,Pocket024,Sketch024,Pad004,Sketch025,DatumPlane005,Sketch026,Pocket029,Chamfer001,Pocket025,Sketch071,Pocket026,DatumPlane,Mirrored001,DatumPlane007,Mirrored002,Pocket027,Sketch068,Pocket028,Mirrored,Pocket030,+14 more]
  Origin = -> Origin001
  Placement = pos=(-38.084,29.963,-79.9617) rot=(0,0,1;1.5708rad)
  Tip = -> Pocket034
FEATURE [PartDesign::SubShapeBinder] Binder001
  BindCopyOnChange = 0
  BindMode = 0
  ClaimChildren = false
  Context = -> Body [Binder001.]
  Fuse = false
  MakeFace = true
  OffsetFill = false
  OffsetIntersection = false
  OffsetJoinType = 0
  OffsetOpenResult = false
  PartialLoad = false
  Relative = true
  Support = -> [Body001[Pocket034.Face79,Pocket034.Face74]]
  _Version = 2
FEATURE [PartDesign::Pad] Pad007
  BaseFeature = -> Pad006
  Direction = (-1,3e-16,2e-16)
  Length = 0.8
  Length2 = 10
  Profile = -> Binder001
  Type = 0
FEATURE [PartDesign::Body] Body  label="Yellow Details"
  Group = -> [Binder,Sketch075,Pad005,Pad006,Binder001,Pad007]
  Origin = -> Origin
  Tip = -> Pad007
FEATURE [Part::Compound] Compound  label="Body"
  Links = -> [Body001,Body]
